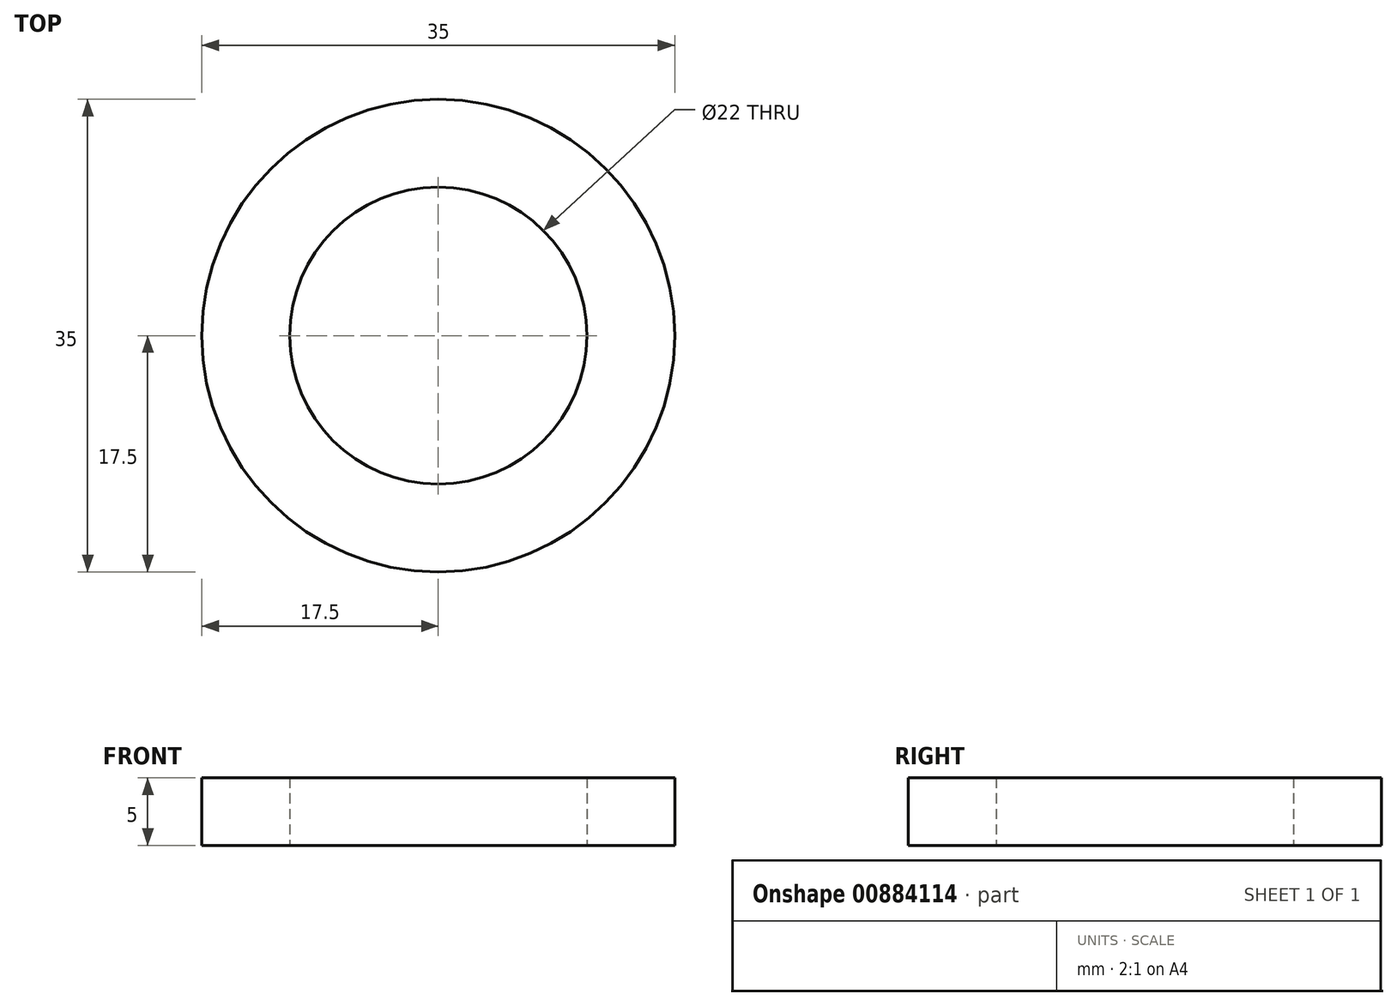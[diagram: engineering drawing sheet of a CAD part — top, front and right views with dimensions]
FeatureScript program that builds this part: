
annotation { "Feature Type Name" : "Feature", "Feature Type Description" : "" }
export const myFeature = defineFeature(function(context is Context, id is Id, definition is map)
    precondition{}
    {
        {
            var Q0;
            Q0=qCreatedBy(makeId("Top.planeOp"),FACE);
            var sketch = newSketch(context, id + "F0", { "sketchPlane" : qUnion([Q0])});
            skCircle(sketch, "E0", {"center": v(0, 0) * mm, "radius": 11 * mm});
            skCircle(sketch, "E1", {"center": v(0, 0) * mm, "radius": 17.5 * mm});
            skSolve(sketch);
        }
        {
            var Q0;
            Q0=qSketchRegion(id+"F0",true);
            extrude(context, id + "F1", {"entities" : qUnion([Q0]), "depth" : 5 * mm, "offsetDistance" : 25 * mm});
        }
    });
